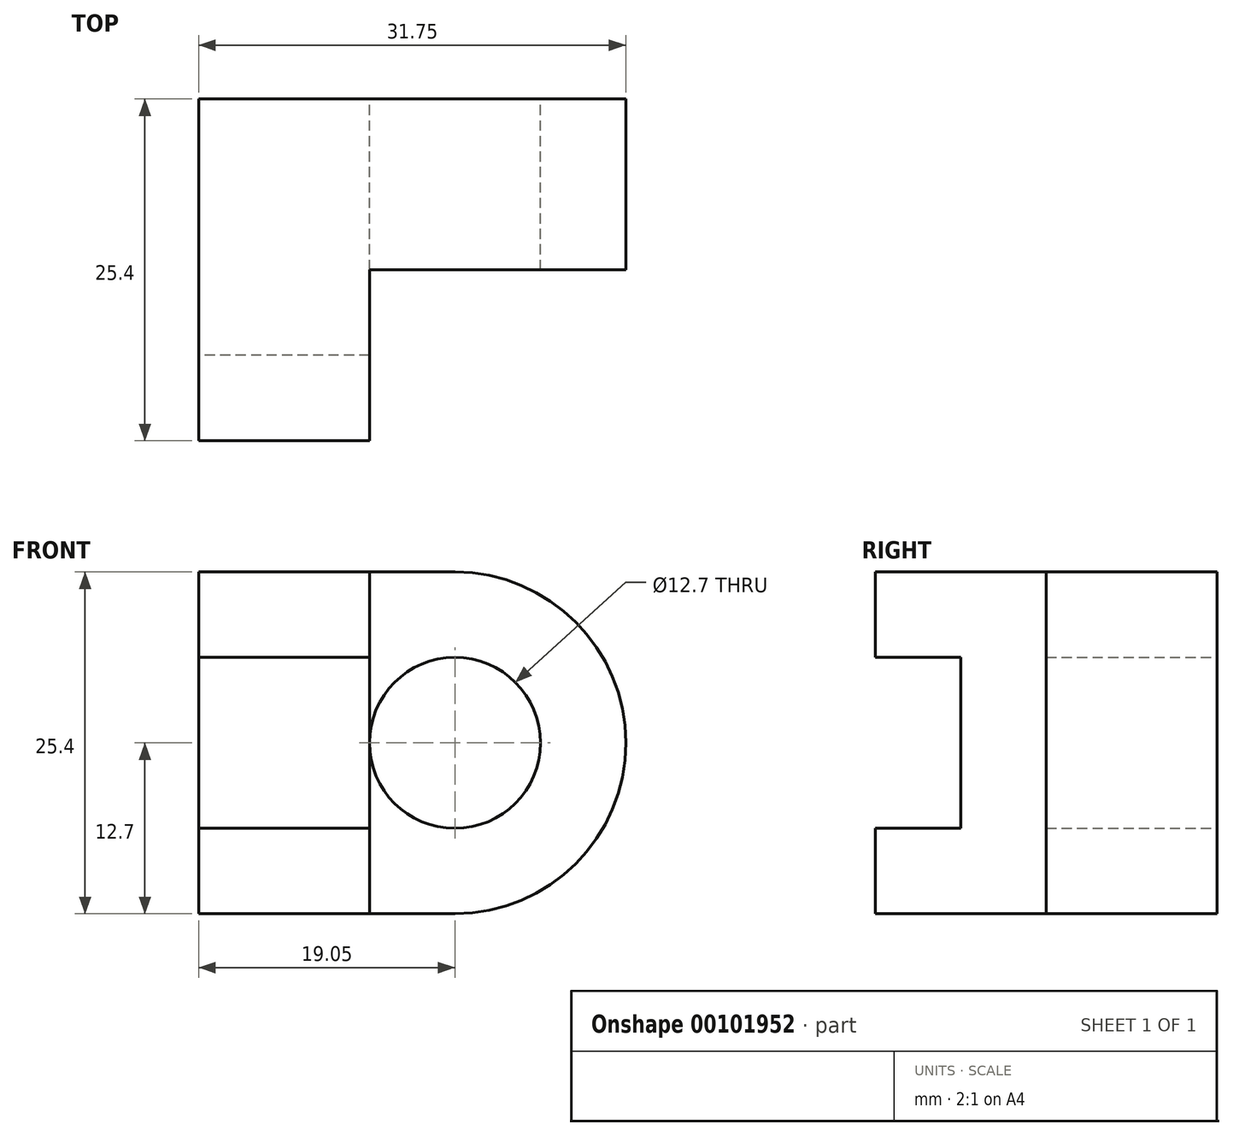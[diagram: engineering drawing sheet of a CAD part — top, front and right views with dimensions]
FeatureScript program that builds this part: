
annotation { "Feature Type Name" : "Feature", "Feature Type Description" : "" }
export const myFeature = defineFeature(function(context is Context, id is Id, definition is map)
    precondition{}
    {
        {
            var Q0;
            Q0=qCreatedBy(makeId("Right.planeOp"),FACE);
            var sketch = newSketch(context, id + "F0", { "sketchPlane" : qUnion([Q0])});
            skLineSegment(sketch, "E0", {"start": v(0, 0) * mm, "end": v(0, 25.4) * mm});
            skLineSegment(sketch, "E1", {"start": v(0, 25.4) * mm, "end": v(-25.4, 25.4) * mm});
            skLineSegment(sketch, "E2", {"start": v(-25.4, 25.4) * mm, "end": v(-25.4, 19.05) * mm});
            skLineSegment(sketch, "E3", {"start": v(-25.4, 19.05) * mm, "end": v(-19.05, 19.05) * mm});
            skLineSegment(sketch, "E4", {"start": v(-19.05, 19.05) * mm, "end": v(-19.05, 6.35) * mm});
            skLineSegment(sketch, "E5", {"start": v(-19.05, 6.35) * mm, "end": v(-25.4, 6.35) * mm});
            skLineSegment(sketch, "E6", {"start": v(-25.4, 6.35) * mm, "end": v(-25.4, 0) * mm});
            skLineSegment(sketch, "E7", {"start": v(-25.4, 0) * mm, "end": v(0, 0) * mm});
            skSolve(sketch);
        }
        {
            var Q0;
            Q0=makeQuery(id+"F0.imprint","IMPRINT",FACE,{"disambiguationData":[TD([[makeQuery(id+"F0.imprint","IMPRINT",EDGE,{"derivedFrom":sQuery(id+"F0.wireOp",EDGE,"E0")}),1.0]])]});
            extrude(context, id + "F1", {"entities" : qUnion([Q0]), "depth" : 12.7 * mm});
        }
        {
            var Q0;
            Q0=makeQuery(id+"F1.opExtrude","SWEPT_FACE",FACE,{"disambiguationData":[OSD([sQuery(id+"F0.wireOp",EDGE,"E0")])]});
            var sketch = newSketch(context, id + "F2", { "sketchPlane" : qUnion([Q0])});
            skLineSegment(sketch, "E8.bottom", {"start": v(-12.7, 0) * mm, "end": v(-19.05, 0) * mm});
            skLineSegment(sketch, "E8.top", {"start": v(-12.7, 25.4) * mm, "end": v(-19.05, 25.4) * mm});
            skLineSegment(sketch, "E8.left", {"start": v(-12.7, 0) * mm, "end": v(-12.7, 25.4) * mm});
            skLineSegment(sketch, "E8.right", {"start": v(-19.05, 0) * mm, "end": v(-19.05, 25.4) * mm});
            skSolve(sketch);
        }
        {
            var Q0;
            Q0=makeQuery(id+"F2.imprint","IMPRINT",FACE,{"disambiguationData":[TD([[makeQuery(id+"F2.imprint","IMPRINT",EDGE,{"derivedFrom":sQuery(id+"F2.wireOp",EDGE,"E8.bottom")}),-1.0]])]});
            extrude(context, id + "F3", {"entities" : qUnion([Q0]), "operationType" : NewBodyOperationType.ADD, "oppositeDirection" : true, "depth" : 12.7 * mm});
        }
        {
            var Q0;
            Q0=makeQuery(id+"F3.boolean.opBoolean","MERGE",FACE,{"derivedFrom":[makeQuery(id+"F1.opExtrude","SWEPT_FACE",FACE,{"disambiguationData":[OSD([sQuery(id+"F0.wireOp",EDGE,"E0")])]}),makeQuery(id+"F3.opExtrude","CAP_FACE",FACE,{"disambiguationData":[OSD([sQuery(id+"F2.wireOp",EDGE,"E8.bottom"),sQuery(id+"F2.wireOp",EDGE,"E8.top"),sQuery(id+"F2.wireOp",EDGE,"E8.left"),sQuery(id+"F2.wireOp",EDGE,"E8.right")])],"isStart":true})]});
            var sketch = newSketch(context, id + "F4", { "sketchPlane" : qUnion([Q0])});
            skArc(sketch, "E9", {"start": v(-19.05, 25.4) * mm, "mid": v(-31.75, 12.7) * mm, "end": v(-19.05, 0) * mm});
            skSolve(sketch);
        }
        {
            var Q0;
            Q0 = qSketchRegion(id + "F4", true);
            var Q1;
            Q1=makeQuery(id+"F4.imprint","IMPRINT",FACE,{"disambiguationData":[TD([[makeQuery(id+"F4.imprint","IMPRINT",EDGE,{"derivedFrom":sQuery(id+"F4.wireOp",EDGE,"E9")}),1.0]])]});
            extrude(context, id + "F5", {"entities" : qUnion([Q0, Q1]), "operationType" : NewBodyOperationType.ADD, "oppositeDirection" : true, "depth" : 12.7 * mm});
        }
        {
            var Q0;
            {var subQ0=sQuery(id+"F2.wireOp",EDGE,"E8.right");Q0=makeQuery(id+"F5.boolean.opBoolean","MERGE",FACE,{"derivedFrom":[makeQuery(id+"F3.boolean.opBoolean","MERGE",FACE,{"derivedFrom":[makeQuery(id+"F1.opExtrude","SWEPT_FACE",FACE,{"disambiguationData":[OSD([sQuery(id+"F0.wireOp",EDGE,"E0")])]}),makeQuery(id+"F3.opExtrude","CAP_FACE",FACE,{"disambiguationData":[OSD([sQuery(id+"F2.wireOp",EDGE,"E8.bottom"),sQuery(id+"F2.wireOp",EDGE,"E8.top"),sQuery(id+"F2.wireOp",EDGE,"E8.left"),subQ0])],"isStart":true})]}),makeQuery(id+"F5.opExtrude","CAP_FACE",FACE,{"disambiguationData":[OSD([subQ0,sQuery(id+"F4.wireOp",EDGE,"E9")])],"isStart":true})]});}
            var sketch = newSketch(context, id + "F6", { "sketchPlane" : qUnion([Q0])});
            skCircle(sketch, "E10", {"center": v(-19.05, 12.7) * mm, "radius": 6.35 * mm});
            skSolve(sketch);
        }
        {
            var Q0;
            Q0=makeQuery(id+"F6.imprint","IMPRINT",FACE,{"disambiguationData":[TD([[makeQuery(id+"F6.imprint","IMPRINT",EDGE,{"derivedFrom":sQuery(id+"F6.wireOp",EDGE,"E10")}),1.0]])]});
            extrude(context, id + "F7", {"entities" : qUnion([Q0]), "operationType" : NewBodyOperationType.REMOVE, "oppositeDirection" : true, "depth" : 12.7 * mm});
        }
    });
